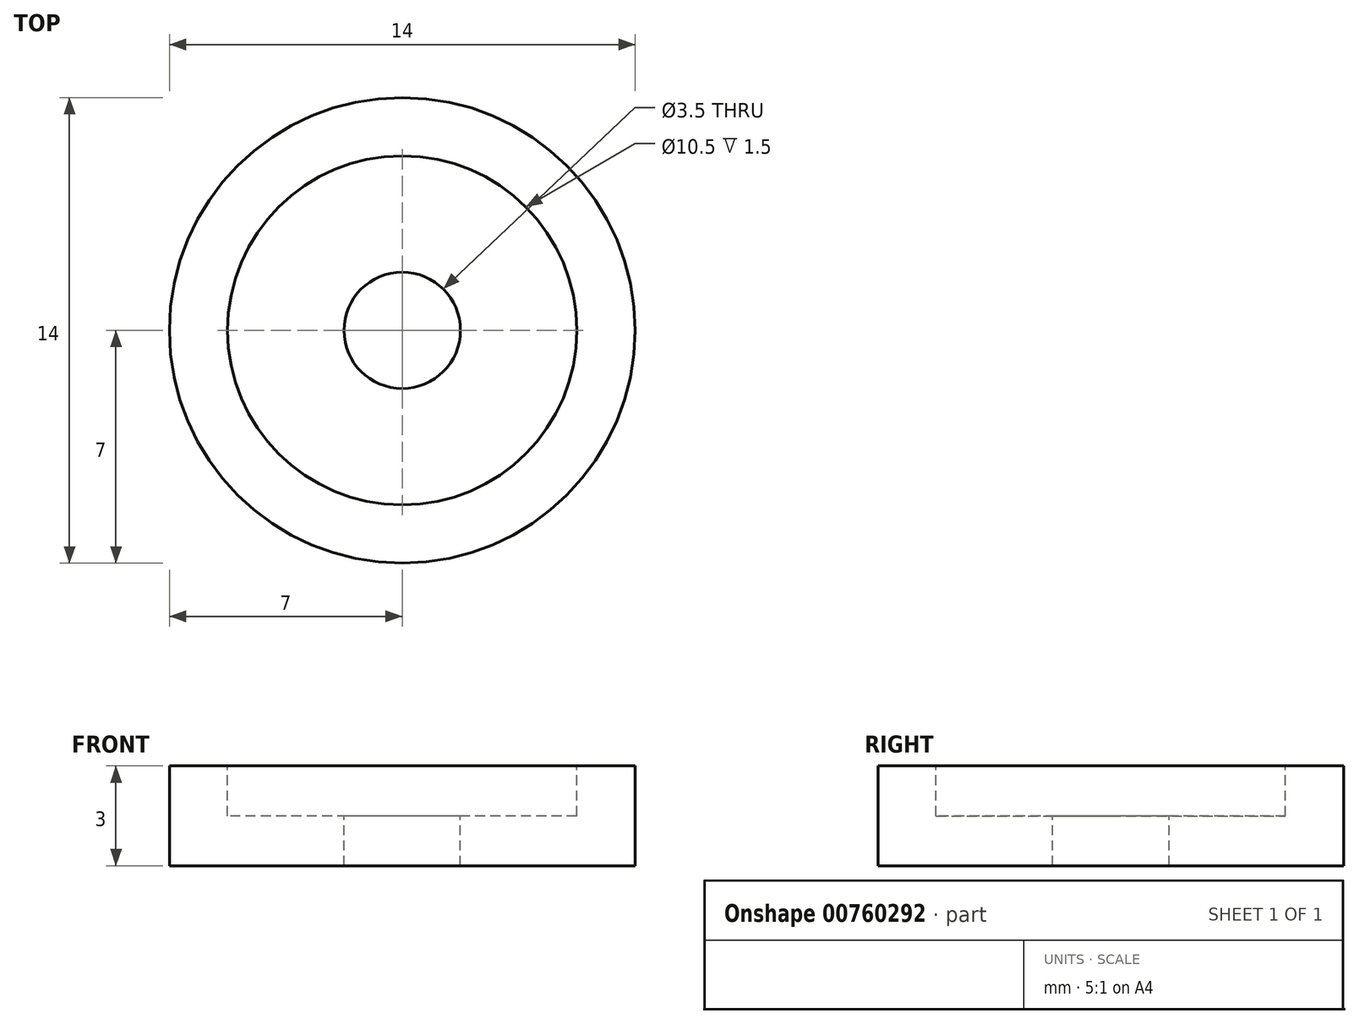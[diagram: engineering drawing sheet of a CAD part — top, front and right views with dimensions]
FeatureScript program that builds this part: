
annotation { "Feature Type Name" : "Feature", "Feature Type Description" : "" }
export const myFeature = defineFeature(function(context is Context, id is Id, definition is map)
    precondition{}
    {
        {
            var Q0;
            Q0=qCreatedBy(makeId("Right.planeOp"),FACE);
            var sketch = newSketch(context, id + "F0", { "sketchPlane" : qUnion([Q0])});
            skLineSegment(sketch, "E0", {"start": v(0, 3.05) * mm, "end": v(0, -0.48) * mm, "construction": true});
            skLineSegment(sketch, "E1", {"start": v(1.75, 0) * mm, "end": v(7, 0) * mm});
            skLineSegment(sketch, "E2", {"start": v(7, 0) * mm, "end": v(7, 3) * mm});
            skLineSegment(sketch, "E3", {"start": v(7, 3) * mm, "end": v(5.25, 3) * mm});
            skLineSegment(sketch, "E4", {"start": v(5.25, 3) * mm, "end": v(5.25, 1.5) * mm});
            skLineSegment(sketch, "E5", {"start": v(5.25, 1.5) * mm, "end": v(1.75, 1.5) * mm});
            skLineSegment(sketch, "E6", {"start": v(1.75, 1.5) * mm, "end": v(1.75, 0) * mm});
            skSolve(sketch);
        }
        {
            var Q0;
            Q0 = qSketchRegion(id + "F0", true);
            var Q1;
            Q1=sQuery(id+"F0.wireOp",EDGE,"E0");
            revolve(context, id + "F1", {"surfaceOperationType" : NewSurfaceOperationType.NEW, "entities" : qUnion([Q0]), "axis" : qUnion([Q1]), "revolveType" : RevolveType.FULL});
        }
    });
